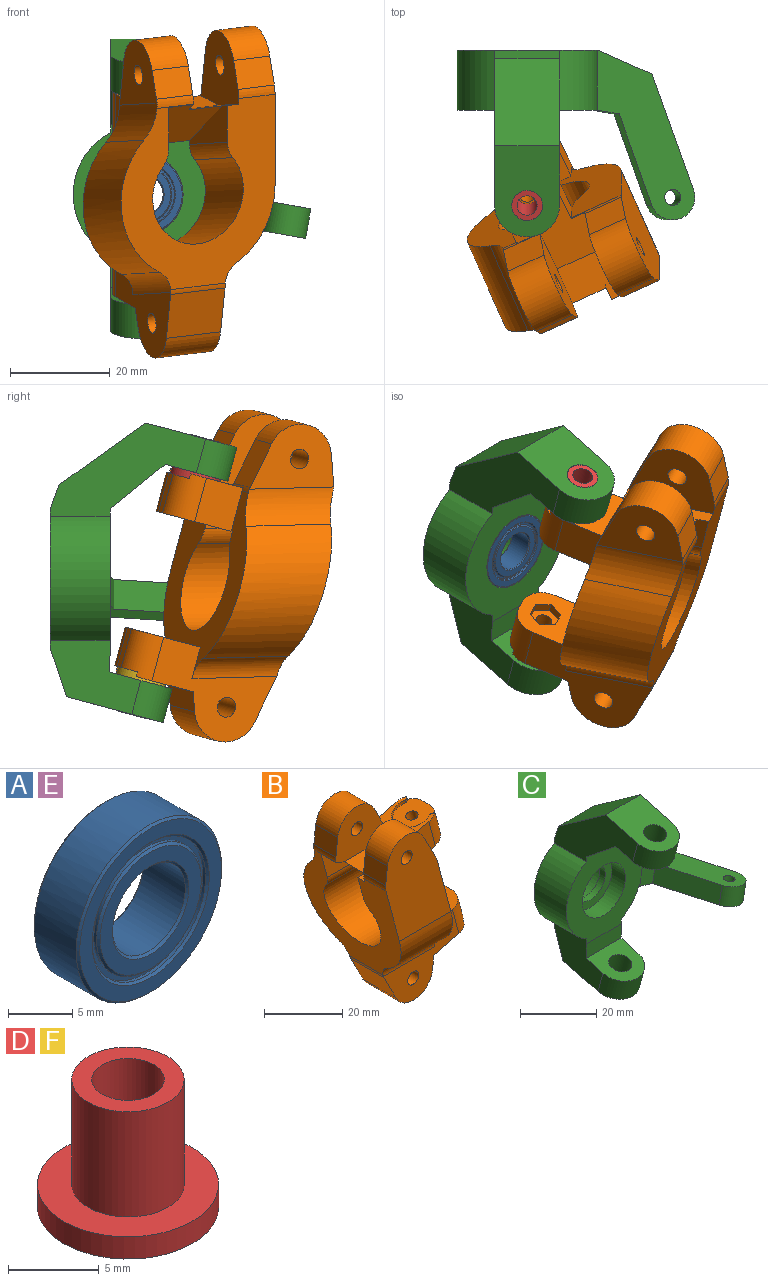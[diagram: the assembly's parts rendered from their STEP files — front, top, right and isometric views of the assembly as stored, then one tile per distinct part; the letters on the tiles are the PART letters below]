
ASSEMBLY  parts=6 mates=5
PART A: 20 faces, bbox 16x5x16 mm
  f0: cylinder r=8mm len=16mm, axis (0,-1,0), area 231.2mm2, adj f1,f2
  f1: cone r=8mm half-angle=45deg, axis (0,1,0), area 14mm2, adj f0,f14
  f2: cone r=8mm half-angle=45deg, axis (0,-1,0), area 14mm2, adj f0,f15
  f3: cone r=6.45mm half-angle=45deg, axis (0,-1,0), area 11.3mm2, adj f5,f14
  f4: cone r=6.45mm half-angle=45deg, axis (0,1,0), area 11.3mm2, adj f6,f15
  f5: cylinder r=6.25mm len=12.5mm, axis (0,-1,0), area 11.8mm2, adj f3,f16
  f6: cylinder r=6.25mm len=12.5mm, axis (0,-1,0), area 11.8mm2, adj f4,f17
  f7: cylinder r=5.75mm len=11.5mm, axis (0,-1,0), area 10.8mm2, adj f9,f16
  f8: cylinder r=5.75mm len=11.5mm, axis (0,-1,0), area 10.8mm2, adj f10,f17
  f9: cone r=5.75mm half-angle=45deg, axis (0,1,0), area 10mm2, adj f7,f18
  f10: cone r=5.75mm half-angle=45deg, axis (0,-1,0), area 10mm2, adj f8,f19
  f11: cone r=4.2mm half-angle=45deg, axis (0,-1,0), area 7.3mm2, adj f13,f18
  f12: cone r=4.2mm half-angle=45deg, axis (0,1,0), area 7.3mm2, adj f13,f19
  f13: cylinder r=4mm len=8mm, axis (0,-1,0), area 115.6mm2, adj f11,f12
  f14: plane 15.6x15.6mm, normal (0,-1,0), area 60.4mm2, adj f1,f3
  f15: plane 15.6x15.6mm, normal (0,1,0), area 60.4mm2, adj f2,f4
  f16: plane 12.5x12.5mm, normal (0,-1,0), area 18.8mm2, adj f5,f7
  f17: plane 12.5x12.5mm, normal (0,1,0), area 18.8mm2, adj f6,f8
  f18: plane 11.1x11.1mm, normal (0,-1,0), area 41.4mm2, adj f9,f11
  f19: plane 11.1x11.1mm, normal (0,1,0), area 41.4mm2, adj f10,f12
PART B: 77 faces, bbox 42.3x34x64 mm
  f0: cylinder r=1.6mm len=6.82mm, axis (-0.26,0,0.97), area 62.3mm2, adj f56,f57
  f1: cylinder r=1.6mm len=6.82mm, axis (-0.26,0,0.97), area 62.3mm2, adj f43,f44
  f2: plane 12.84x12mm, normal (0.26,0,-0.97), area 122.6mm2, adj f3,f13,f14,f34,f45,f46,f47,f48
  f3: plane 7.73x2.07mm, normal (0.97,0,0.26), area 16mm2, adj f2,f43,f69,f70
  f4: plane 19.08x15mm, normal (-0.26,0,0.97), area 144.9mm2, adj f5,f6,f7,f13,f14,f38,f39,f40
  f5: plane 10.09x10mm, normal (0,0,1), area 81.8mm2, adj f4,f6,f7,f11,f33,f34
  f6: plane 18.49x15.03mm, normal (0,1,0), area 194.6mm2, adj f4,f5,f11,f18,f19,f20,f25,f73
  f7: plane 18.49x15.03mm, normal (0,-1,0), area 193.3mm2, adj f4,f5,f8,f11,f21,f22,f26,f34
  f8: plane 8.71x8mm, normal (0.89,0,0.45), area 78.3mm2, adj f7,f22,f28,f64
  f9: plane 37.54x34mm, normal (0.97,0,0.26), area 567.7mm2, adj f12,f13,f14,f15,f16,f17,f27,f29
  f10: plane 12x4.05mm, normal (0.99,0,-0.11), area 48.9mm2, adj f17,f23,f27,f37
  f11: plane 36.58x34mm, normal (-0.97,0,-0.26), area 622.7mm2, adj f5,f6,f7,f12,f15,f16,f29,f32
  f12: cylinder r=10mm len=23.05mm, axis (1,0,0), area 845.3mm2, adj f9,f11,f65,f66
  f13: plane 10.84x10.48mm, normal (0,-1,0), area 75.6mm2, adj f2,f4,f9,f34,f70,f73
  f14: plane 10.84x10.48mm, normal (0,1,0), area 75.6mm2, adj f2,f4,f9,f34,f64,f69
  f15: cylinder r=17mm len=22.58mm, axis (1,0,0), area 331.7mm2, adj f9,f11,f16,f76
  f16: plane 32x23.65mm, normal (0,-1,0), area 520mm2, adj f9,f11,f15,f18,f19,f20,f25,f73
  f17: plane 27.36x21.41mm, normal (0,-1,0), area 241.9mm2, adj f9,f10,f23,f24,f30,f36,f37,f68
  f18: plane 8x5.84mm, normal (-0.99,0,0.11), area 47mm2, adj f6,f16,f19,f74
  f19: cylinder r=7mm len=13.19mm, axis (0,1,0), area 143.3mm2, adj f6,f16,f18,f20
  f20: plane 8.71x8mm, normal (0.89,0,0.45), area 78.3mm2, adj f6,f16,f19,f73
  f21: plane 8x5.84mm, normal (-0.99,0,0.11), area 47mm2, adj f7,f22,f28,f71
  f22: cylinder r=7mm len=13.19mm, axis (0,1,0), area 143.3mm2, adj f7,f8,f21,f28
  f23: cylinder r=7mm len=13.19mm, axis (0,1,0), area 214.9mm2, adj f10,f17,f24,f27
  f24: plane 12x8.71mm, normal (-0.89,0,-0.45), area 117.4mm2, adj f17,f23,f27,f72
  f25: cylinder r=2mm len=8mm, axis (0,1,0), area 100.5mm2, adj f6,f16
  f26: cylinder r=2mm len=8mm, axis (0,1,0), area 100.5mm2, adj f7,f28
  f27: plane 27.36x21.41mm, normal (0,1,0), area 241.9mm2, adj f9,f10,f23,f24,f30,f36,f37,f67
  f28: plane 18.46x12.82mm, normal (0,1,0), area 162.6mm2, adj f8,f21,f22,f26,f35,f64,f71
  f29: cylinder r=17mm len=26.8mm, axis (1,0,0), area 582.1mm2, adj f9,f11,f35,f75
  f30: cylinder r=2mm len=12mm, axis (0,1,0), area 150.8mm2, adj f17,f27
  f31: plane 7.73x2.07mm, normal (0.97,0,0.26), area 16mm2, adj f36,f56,f67,f68
  f32: plane 20.88x8.37mm, normal (0,-1,0), area 85.9mm2, adj f9,f11,f34,f65
  f33: plane 20.6x7.34mm, normal (0,1,0), area 84.6mm2, adj f5,f9,f11,f34,f66
  f34: plane 20.77x13mm, normal (-0.34,0,-0.94), area 264.6mm2, adj f2,f5,f7,f9,f11,f13,f14,f32
  f35: cylinder r=10mm len=20.41mm, axis (1,0,0), area 147.2mm2, adj f9,f11,f28,f29,f64,f71
  f36: plane 12.94x12mm, normal (-0.26,0,0.97), area 123.9mm2, adj f9,f17,f27,f31,f58,f59,f60,f61
  f37: plane 12.07x12mm, normal (0.26,0,-0.97), area 74.3mm2, adj f10,f17,f27,f51,f52,f53,f54,f55
  f38: cylinder r=2mm len=1.12mm, axis (-0.26,0,0.97), area 0.7mm2, adj f4,f39,f43,f69
  f39: cylinder r=0.6mm len=1.13mm, axis (-0.26,0,0.97), area 0.7mm2, adj f4,f38,f40,f43
  f40: cylinder r=5.05mm len=10.1mm, axis (-0.26,0,0.97), area 20.6mm2, adj f4,f39,f41,f43
  f41: cylinder r=0.6mm len=1.13mm, axis (-0.26,0,0.97), area 0.7mm2, adj f4,f40,f42,f43
  f42: cylinder r=2mm len=1.12mm, axis (-0.26,0,0.97), area 0.7mm2, adj f4,f41,f43,f70
  f43: plane 10.1x10.09mm, normal (-0.26,0,0.97), area 79.7mm2, adj f1,f3,f38,f39,f40,f41,f42,f69
  f44: plane 6.35x5.31mm, normal (0.26,0,-0.97), area 18.2mm2, adj f1,f45,f46,f47,f48,f49,f50
  f45: plane 3.18x1.74mm, normal (-0.97,0,-0.26), area 5.7mm2, adj f2,f44,f46,f50
  f46: plane 3.12x2.45mm, normal (-0.48,0.87,-0.13), area 5.7mm2, adj f2,f44,f45,f47
  f47: plane 3.12x2.45mm, normal (0.48,0.87,0.13), area 5.7mm2, adj f2,f44,f46,f48
  f48: plane 3.18x1.74mm, normal (0.97,0,0.26), area 5.7mm2, adj f2,f44,f47,f49
  f49: plane 3.12x2.45mm, normal (0.48,-0.87,0.13), area 5.7mm2, adj f2,f44,f48,f50
  f50: plane 3.12x2.45mm, normal (-0.48,-0.87,-0.13), area 5.7mm2, adj f2,f44,f45,f49
  f51: cylinder r=2mm len=1.12mm, axis (0.26,0,-0.97), area 0.7mm2, adj f37,f52,f56,f68
  f52: cylinder r=0.6mm len=1.13mm, axis (0.26,0,-0.97), area 0.7mm2, adj f37,f51,f53,f56
  f53: cylinder r=5.05mm len=10.1mm, axis (0.26,0,-0.97), area 20.6mm2, adj f37,f52,f54,f56
  f54: cylinder r=0.6mm len=1.13mm, axis (0.26,0,-0.97), area 0.7mm2, adj f37,f53,f55,f56
  f55: cylinder r=2mm len=1.12mm, axis (0.26,0,-0.97), area 0.7mm2, adj f37,f54,f56,f67
  f56: plane 10.1x10.09mm, normal (0.26,0,-0.97), area 79.7mm2, adj f0,f31,f51,f52,f53,f54,f55,f67
  f57: plane 6.35x5.31mm, normal (-0.26,0,0.97), area 18.2mm2, adj f0,f58,f59,f60,f61,f62,f63
  f58: plane 3.18x1.74mm, normal (-0.97,0,-0.26), area 5.7mm2, adj f36,f57,f59,f63
  f59: plane 3.12x2.45mm, normal (-0.48,-0.87,-0.13), area 5.7mm2, adj f36,f57,f58,f60
  f60: plane 3.12x2.45mm, normal (0.48,-0.87,0.13), area 5.7mm2, adj f36,f57,f59,f61
  f61: plane 3.18x1.74mm, normal (0.97,0,0.26), area 5.7mm2, adj f36,f57,f60,f62
  f62: plane 3.12x2.45mm, normal (0.48,0.87,0.13), area 5.7mm2, adj f36,f57,f61,f63
  f63: plane 3.12x2.45mm, normal (-0.48,0.87,-0.13), area 5.7mm2, adj f36,f57,f58,f62
  f64: cylinder r=5mm len=8.02mm, axis (0,1,0), area 5.2mm2, adj f4,f7,f8,f9,f14,f28,f35
  f65: cylinder r=5mm len=19.5mm, axis (1,0,0), area 65mm2, adj f9,f11,f12,f32
  f66: cylinder r=5mm len=19.5mm, axis (1,0,0), area 65mm2, adj f9,f11,f12,f33
  f67: cylinder r=5mm len=9.99mm, axis (0.26,0,-0.97), area 66.2mm2, adj f27,f31,f36,f37,f55,f56
  f68: cylinder r=5mm len=9.99mm, axis (0.26,0,-0.97), area 66.2mm2, adj f17,f31,f36,f37,f51,f56
  f69: cylinder r=5mm len=9.99mm, axis (-0.26,0,0.97), area 66.2mm2, adj f2,f3,f4,f14,f38,f43
  f70: cylinder r=5mm len=9.99mm, axis (0.26,0,-0.97), area 66.2mm2, adj f2,f3,f4,f13,f42,f43
  f71: cylinder r=5mm len=8.06mm, axis (0,-1,0), area 14.9mm2, adj f7,f11,f21,f28,f35
  f72: cylinder r=5mm len=12.06mm, axis (0,1,0), area 12.6mm2, adj f11,f17,f24,f27,f75,f76
  f73: cylinder r=5mm len=11mm, axis (0,1,0), area 10.3mm2, adj f4,f6,f9,f13,f16,f20
  f74: cylinder r=5mm len=8mm, axis (0,-1,0), area 14.9mm2, adj f6,f11,f16,f18
  f75: cylinder r=5mm len=19.8mm, axis (1,0,0), area 97.6mm2, adj f9,f11,f27,f29,f72
  f76: cylinder r=5mm len=19.8mm, axis (1,0,0), area 97.6mm2, adj f9,f11,f15,f17,f72
PART C: 35 faces, bbox 47.6x37.3x59.9 mm
  f0: cylinder r=14mm len=12mm, axis (0,1,0), area 175.8mm2, adj f3,f4,f9,f23
  f1: cylinder r=14mm len=12mm, axis (0,1,0), area 117.2mm2, adj f3,f4,f12,f22
  f2: cylinder r=14mm len=24.8mm, axis (0,1,0), area 365.6mm2, adj f3,f4,f11,f13
  f3: plane 28.31x28mm, normal (0,-1,0), area 428.9mm2, adj f0,f1,f2,f5,f9,f11,f12,f13
  f4: plane 28.31x28mm, normal (0,1,0), area 428.9mm2, adj f0,f1,f2,f9,f10,f11,f12,f13
  f5: plane 13x10.97mm, normal (0,-0.63,-0.78), area 183.1mm2, adj f3,f6,f9,f11
  f6: plane 13x12.56mm, normal (0,0.26,-0.97), area 120.7mm2, adj f5,f9,f11,f18,f21
  f7: plane 18.23x13mm, normal (0,-0.26,0.97), area 197mm2, adj f8,f9,f11,f18,f21
  f8: plane 17.4x13mm, normal (0,0.58,0.81), area 277.8mm2, adj f7,f9,f10,f11
  f9: plane 31.06x18.71mm, normal (1,0,0), area 280.7mm2, adj f0,f3,f4,f5,f6,f7,f8,f10
  f10: plane 13x4.7mm, normal (0,0.94,0.34), area 65mm2, adj f4,f8,f9,f11
  f11: plane 31.06x18.71mm, normal (-1,0,0), area 280.7mm2, adj f2,f3,f4,f5,f6,f7,f8,f10
  f12: plane 18.12x14.75mm, normal (1,0,0), area 166.9mm2, adj f1,f3,f4,f14,f15,f16,f17,f19
  f13: plane 18.12x14.75mm, normal (-1,0,0), area 166.9mm2, adj f2,f3,f4,f14,f15,f16,f17,f19
  f14: plane 13x4.7mm, normal (0,-1,-0.03), area 61.2mm2, adj f3,f12,f13,f15
  f15: plane 13x12.56mm, normal (0,-0.26,0.97), area 120.7mm2, adj f12,f13,f14,f19,f20
  f16: plane 19.32x13mm, normal (0,0.26,-0.97), area 211.7mm2, adj f12,f13,f17,f19,f20
  f17: plane 13x9.65mm, normal (0,0.95,-0.32), area 132.5mm2, adj f4,f12,f13,f16
  f18: cylinder r=6.5mm len=13mm, axis (0,-0.26,0.97), area 142.9mm2, adj f6,f7,f9,f11
  f19: cylinder r=6.5mm len=13mm, axis (0,-0.26,0.97), area 142.9mm2, adj f12,f13,f15,f16
  f20: cylinder r=3.1mm len=8.37mm, axis (0,0.26,-0.97), area 136.3mm2, adj f15,f16
  f21: cylinder r=3.1mm len=8.37mm, axis (0,0.26,-0.97), area 136.3mm2, adj f6,f7
  f22: plane 33.91x19.57mm, normal (-0.17,0,-0.98), area 309.8mm2, adj f1,f3,f4,f24,f25,f26,f27,f28
  f23: plane 33.91x19.57mm, normal (0.17,0,0.98), area 309.8mm2, adj f0,f3,f4,f24,f25,f26,f27,f28
  f24: cylinder r=4.5mm len=9.64mm, axis (0.17,0,0.98), area 84.8mm2, adj f22,f23,f25,f29
  f25: plane 23.11x9.33mm, normal (0.93,0.34,-0.16), area 147.6mm2, adj f22,f23,f24,f26
  f26: plane 11.73x7.79mm, normal (0.4,0.92,-0.07), area 71.1mm2, adj f4,f22,f23,f25
  f27: plane 6.63x5.16mm, normal (-0.17,-0.99,0.03), area 25.4mm2, adj f3,f22,f23,f29
  f28: cylinder r=1.6mm len=6.46mm, axis (0.17,0,0.98), area 60.3mm2, adj f22,f23
  f29: plane 18.23x7.58mm, normal (-0.93,-0.34,0.16), area 116.4mm2, adj f22,f23,f24,f27
  f30: cylinder r=8mm len=16mm, axis (0,1,0), area 251.3mm2, adj f4,f31
  f31: plane 16x16mm, normal (0,1,0), area 106mm2, adj f30,f32
  f32: cylinder r=5.5mm len=11mm, axis (0,1,0), area 69.1mm2, adj f31,f33
  f33: plane 16x16mm, normal (0,-1,0), area 106mm2, adj f32,f34
  f34: cylinder r=8mm len=16mm, axis (0,1,0), area 251.3mm2, adj f3,f33
PART D: 6 faces, bbox 10x10x8.6 mm
  f0: plane 10x10mm, normal (0,0,-1), area 66mm2, adj f1,f5
  f1: cylinder r=2mm len=8.6mm, axis (0,0,-1), area 108.1mm2, adj f0,f2
  f2: plane 6.2x6.2mm, normal (0,0,1), area 17.6mm2, adj f1,f3
  f3: cylinder r=3.1mm len=7.1mm, axis (0,0,-1), area 138.3mm2, adj f2,f4
  f4: plane 10x10mm, normal (0,0,1), area 48.3mm2, adj f3,f5
  f5: cylinder r=5mm len=10mm, axis (0,0,-1), area 47.1mm2, adj f0,f4
PART E: same geometry as A
PART F: same geometry as D
PLACE A t=(0,-9.5,0)mm
PLACE B rot(axis=(-0.05,-0.05,1),114.3deg) t=(-0.12,-23.18,-0.52)mm
PLACE C rot(axis=(1,0,0),0deg) t=(-40,0,0)mm
PLACE D rot(axis=(1,0,0),15deg) t=(0,-28.86,19.7)mm
PLACE E t=(0,-2.5,0)mm
PLACE F rot(axis=(-1,0,0),165deg) t=(0,-18.51,-18.94)mm
MATE revolute F.f1 <-> C.f18  axis (0,0.26,-0.97) through (0,-18.12,-20.39)mm
MATE fastened D.f1 <-> C.f18  axis (0,-0.26,0.97) through (0,-29.25,21.15)mm
MATE revolute E.f0 <-> A.f0  axis (0,1,0) through (0,0,0)mm
MATE revolute D.f1 <-> B.f0  axis (0,0.26,-0.97) through (0,-28.86,19.7)mm
MATE revolute E.f0 <-> C.f30  axis (0,1,0) through (0,0,0)mm
